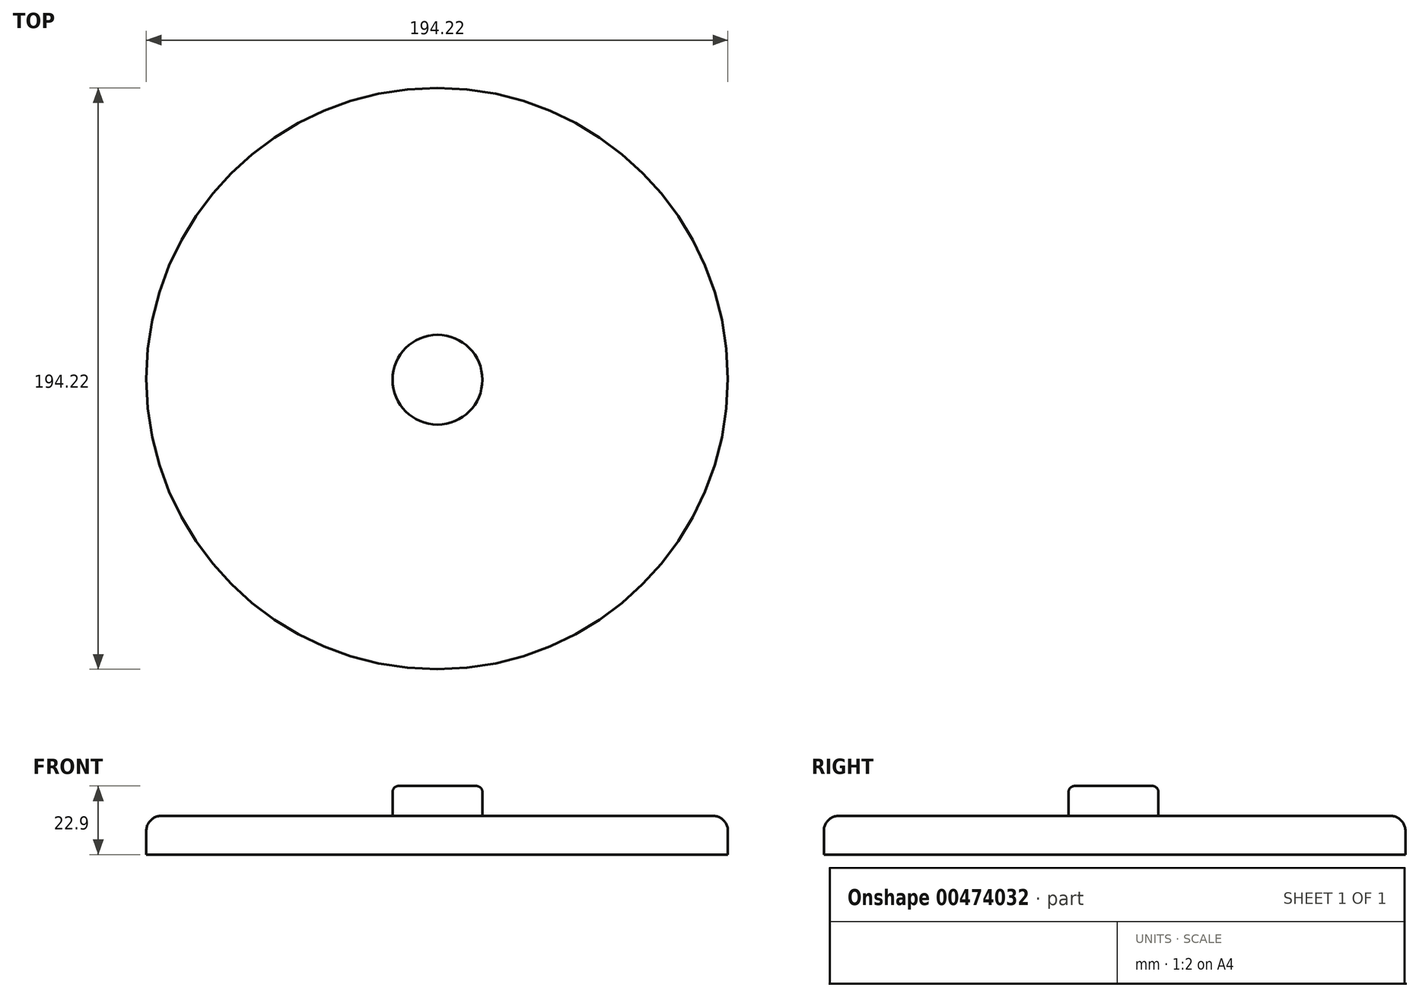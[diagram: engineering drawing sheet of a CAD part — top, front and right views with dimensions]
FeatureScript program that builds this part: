
annotation { "Feature Type Name" : "Feature", "Feature Type Description" : "" }
export const myFeature = defineFeature(function(context is Context, id is Id, definition is map)
    precondition{}
    {
        {
            var Q0;
            Q0=qCreatedBy(makeId("Front.planeOp"),FACE);
            var sketch = newSketch(context, id + "F0", { "sketchPlane" : qUnion([Q0])});
            skLineSegment(sketch, "E0", {"start": v(-97.1, 18.47) * mm, "end": v(0, 18.47) * mm});
            skLineSegment(sketch, "E1", {"start": v(-97.1, 18.47) * mm, "end": v(-97.1, 26.37) * mm});
            skLineSegment(sketch, "E2", {"start": v(-92.1, 31.37) * mm, "end": v(0, 31.37) * mm});
            skLineSegment(sketch, "E3", {"start": v(0, 31.37) * mm, "end": v(0, 18.47) * mm});
            skPoint(sketch, "E4.visualSharp", {"position": v(-97.1, 31.37) * mm});
            skArc(sketch, "E4.filletArc", {"start": v(-92.1, 31.37) * mm, "mid": v(-95.64, 29.9) * mm, "end": v(-97.1, 26.37) * mm});
            skSolve(sketch);
        }
        {
            var Q0;
            Q0 = qSketchRegion(id + "F0", true);
            var Q1;
            Q1=sQuery(id+"F0.wireOp",EDGE,"E3");
            revolve(context, id + "F1", {"entities" : qUnion([Q0]), "axis" : qUnion([Q1]), "revolveType" : RevolveType.FULL});
        }
        {
            var Q0;
            Q0=makeQuery(id+"F1.opRevolve","SWEPT_FACE",FACE,{"disambiguationData":[OSD([sQuery(id+"F0.wireOp",EDGE,"E2")])]});
            var sketch = newSketch(context, id + "F2", { "sketchPlane" : qUnion([Q0])});
            skCircle(sketch, "E5", {"center": v(0.12, -0.37) * mm, "radius": 15 * mm});
            skSolve(sketch);
        }
        {
            var Q0;
            Q0 = qSketchRegion(id + "F2", true);
            extrude(context, id + "F3", {"entities" : qUnion([Q0]), "operationType" : NewBodyOperationType.ADD, "depth" : 10 * mm});
        }
        {
            var Q0;
            Q0=makeQuery(id+"F3.opExtrude","CAP_EDGE",EDGE,{"disambiguationData":[OSD([sQuery(id+"F2.wireOp",EDGE,"E5")])],"isStart":false});
            fillet(context, id + "F4", {"entities" : qUnion([Q0]), "radius" : 2 * mm, "tangentPropagation" : true, "allowEdgeOverflow" : false});
        }
    });
